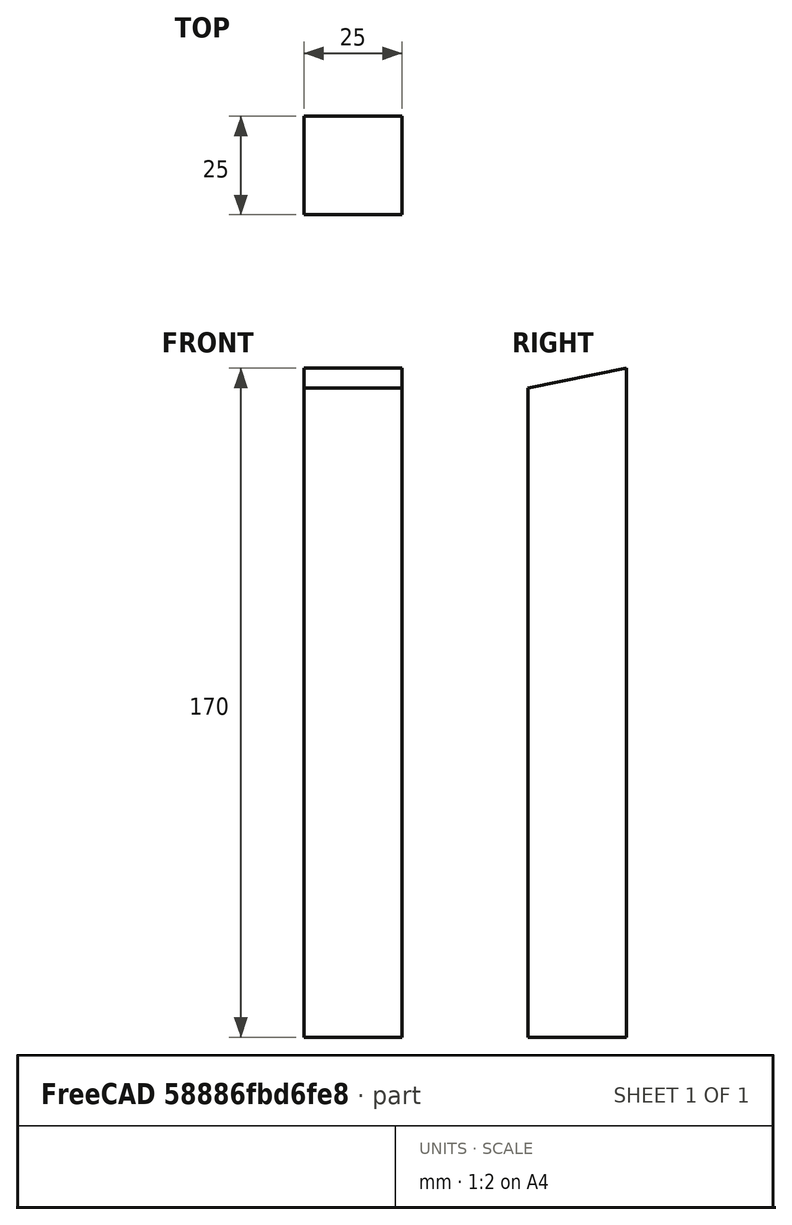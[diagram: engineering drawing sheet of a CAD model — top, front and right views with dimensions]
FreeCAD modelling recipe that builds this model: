
FCSTD DOCUMENT  (FreeCAD 0.19R24366 (Git))
Label: Part3Hollow
License: All rights reserved
LicenseURL: http://en.wikipedia.org/wiki/All_rights_reserved
objects: TechDraw::DrawViewDimension×4, Sketcher::SketchObject×1, PartDesign::Pad×1, PartDesign::Body×1, TechDraw::DrawSVGTemplate×1, TechDraw::DrawViewPart×1, TechDraw::DrawPage×1
note: 4 computed .brp shape members not serialized (recipe doc carries the construction recipe); baked Part::Feature solids carry a one-line shape summary decoded from their .brp

FEATURE [Sketcher::SketchObject] Sketch
  FullyConstrained = true
  MapMode = 5
  Placement = pos=(0,0,0) rot=(0.57735,0.57735,0.57735;2.0944rad)
  Support = -> [YZ_Plane]
  sketch-geometry (4):
    g0: LineSegment StartX=12.5 StartY=85 StartZ=0 EndX=12.5 EndY=-85 EndZ=0
    g1: LineSegment StartX=12.5 StartY=-85 StartZ=0 EndX=-12.5 EndY=-85 EndZ=0
    g2: LineSegment StartX=-12.5 StartY=-85 StartZ=0 EndX=-12.5 EndY=80 EndZ=0
    g3: LineSegment StartX=-12.5 StartY=80 StartZ=0 EndX=12.5 EndY=85 EndZ=0
  constraints (12):
    c: Coincident(g0,g1)
    c: Coincident(g1,g2)
    c: Horizontal(g1)
    c: Vertical(g0)
    c: Vertical(g2)
    c: DistanceX(g2,g0) = 25
    c: DistanceY(g0,g0) = 170
    c: Coincident(g3,g2)
    c: Coincident(g3,g0)
    c: DistanceY(g1,g-1) = 85
    c: DistanceY(g1,g2) = 165
    c: DistanceX(g1,g-1) = 12.5
FEATURE [PartDesign::Pad] Pad
  Direction = (1,1,1)
  Length = 25
  Length2 = 100
  Placement = pos=(0,0,0) rot=(0.57735,0.57735,0.57735;2.0944rad)
  Profile = -> Sketch
  Type = 0
FEATURE [PartDesign::Body] Body
  Group = -> [Sketch,Pad]
  Origin = -> Origin
  Tip = -> Pad
FEATURE [TechDraw::DrawSVGTemplate] Template
  EditableTexts = AUTHOR_NAME=Natan Hari Pamungkas; DN=Part - 03; DRAWING_TITLE=Part Besi Hollow - 03; FC-DATE=18/03/2022; FC-REV=REV A; FC-SC=1; FC-SH=X / Y; FC-SI=A4; FreeCAD_DRAWING=Jumlah item 2; PN=Hollow - 03; SI-1=Besi Hollow Ukuran 2.5 cm x 2.5 cm; SI-2=Ketebalan menyesuaikan
  Height = 297
  Orientation = 0
  Width = 210
FEATURE [TechDraw::DrawViewPart] View  label="Right"
  CoarseView = false
  Direction = (1,0,0)
  Focus = 100
  HardHidden = false
  IsoCount = 0
  IsoHidden = false
  IsoVisible = false
  LockPosition = false
  Perspective = false
  Rotation = 0
  ScaleType = 0
  SeamHidden = false
  SeamVisible = true
  SmoothHidden = false
  SmoothVisible = true
  Source = -> [Body]
  X = 105.471
  XDirection = (0,1,0)
  Y = 174.387
FEATURE [TechDraw::DrawViewDimension] Dimension
  Arbitrary = false
  ArbitraryTolerances = false
  EqualTolerance = true
  FormatSpec = %.2f
  FormatSpecOverTolerance = %+.2f
  FormatSpecUnderTolerance = %+.2f
  Inverted = false
  LockPosition = false
  MeasureType = 1
  OverTolerance = 0
  References2D = -> [View]
  Rotation = 0
  ScaleType = 0
  TheoreticalExact = false
  Type = 0
  UnderTolerance = 0
  X = -2.73403
  Y = 97.6091
FEATURE [TechDraw::DrawViewDimension] Dimension001
  Arbitrary = false
  ArbitraryTolerances = false
  EqualTolerance = true
  FormatSpec = %.2f
  FormatSpecOverTolerance = %+.2f
  FormatSpecUnderTolerance = %+.2f
  Inverted = false
  LockPosition = false
  MeasureType = 1
  OverTolerance = 0
  References2D = -> [View]
  Rotation = 0
  ScaleType = 0
  TheoreticalExact = false
  Type = 2
  UnderTolerance = 0
  X = 36.1319
  Y = 0.429671
FEATURE [TechDraw::DrawViewDimension] Dimension002
  Arbitrary = false
  ArbitraryTolerances = false
  EqualTolerance = true
  FormatSpec = %.2f
  FormatSpecOverTolerance = %+.2f
  FormatSpecUnderTolerance = %+.2f
  Inverted = false
  LockPosition = false
  MeasureType = 1
  OverTolerance = 0
  References2D = -> [View]
  Rotation = 0
  ScaleType = 0
  TheoreticalExact = false
  Type = 1
  UnderTolerance = 0
  X = -2.14836
  Y = -71.2505
FEATURE [TechDraw::DrawViewDimension] Dimension003
  Arbitrary = false
  ArbitraryTolerances = false
  EqualTolerance = true
  FormatSpec = %.2f
  FormatSpecOverTolerance = %+.2f
  FormatSpecUnderTolerance = %+.2f
  Inverted = false
  LockPosition = false
  MeasureType = 1
  OverTolerance = 0
  References2D = -> [View]
  Rotation = 0
  ScaleType = 0
  TheoreticalExact = false
  Type = 2
  UnderTolerance = 0
  X = -34.4132
  Y = -4.64836
FEATURE [TechDraw::DrawPage] Page
  KeepUpdated = true
  NextBalloonIndex = 1
  ProjectionType = 0
  Template = -> Template
  Views = -> [View,Dimension,Dimension001,Dimension002,Dimension003]
